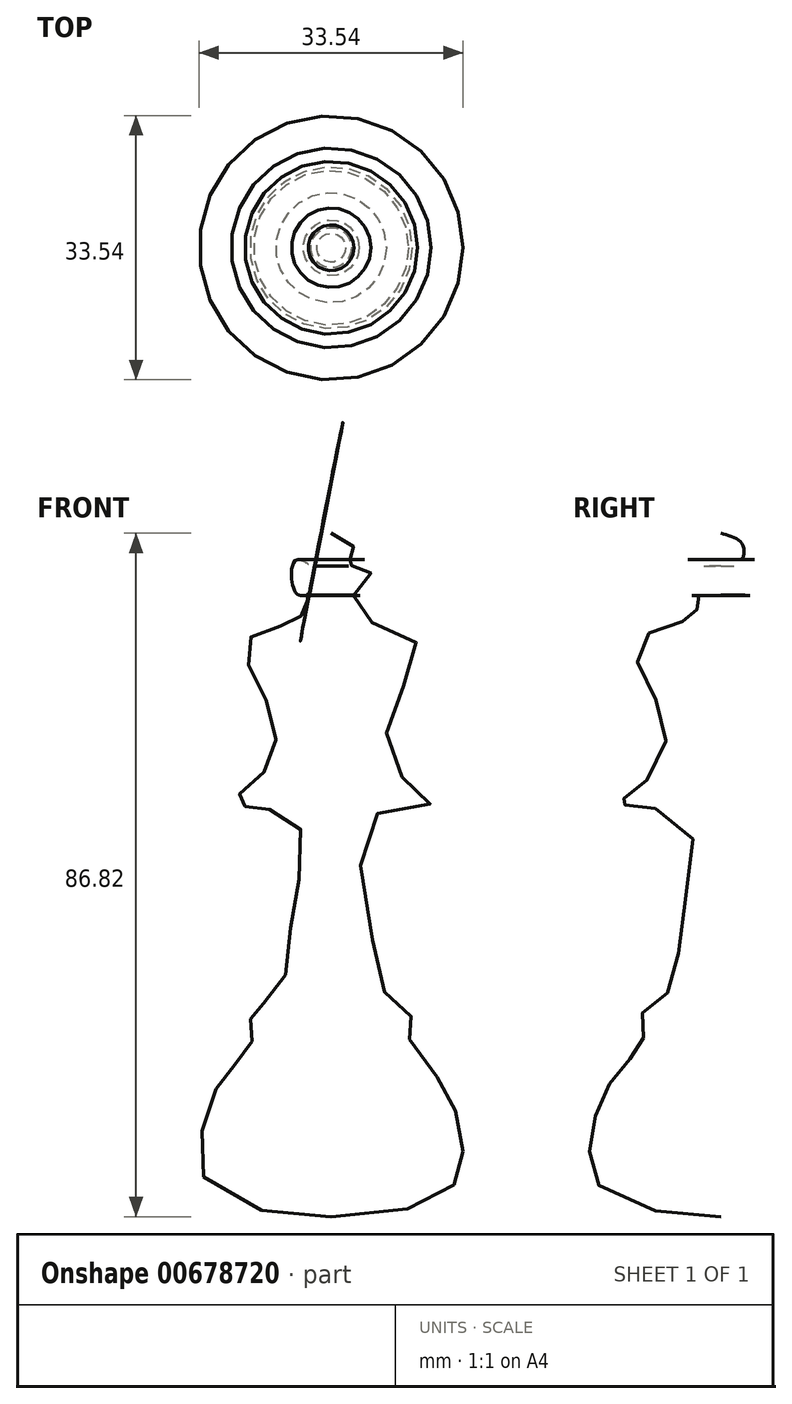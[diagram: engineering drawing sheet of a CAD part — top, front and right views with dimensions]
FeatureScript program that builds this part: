
annotation { "Feature Type Name" : "Feature", "Feature Type Description" : "" }
export const myFeature = defineFeature(function(context is Context, id is Id, definition is map)
    precondition{}
    {
        {
            var Q0;
            Q0=qCreatedBy(makeId("Front.planeOp"),FACE);
            var sketch = newSketch(context, id + "F0", { "sketchPlane" : qUnion([Q0])});
            skFitSpline(sketch, "E0", {"points": [v(0, 66.18) * mm, v(2.46, 65.16) * mm, v(2.88, 64.25) * mm, v(2.9, 63.57) * mm, v(2.76, 63.07) * mm, v(2.2, 62.77) * mm, v(1.89, 62.77) * mm, v(1.96, 62.1) * mm, v(2.72, 62.17) * mm, v(4.59, 62.72) * mm, v(4.35, 58.48) * mm, v(2.74, 58.25) * mm, v(3.92, 55.56) * mm, v(10.61, 52.62) * mm, v(9.54, 47.53) * mm, v(7.02, 40.7) * mm, v(9.43, 34.81) * mm, v(12.64, 31.87) * mm, v(4.88, 30) * mm, v(4.9, 17.88) * mm, v(6.66, 8) * mm, v(9.84, 5.46) * mm, v(10.16, 3.23) * mm, v(9.84, 2.28) * mm, v(13.03, -2.34) * mm, v(15.42, -6) * mm, v(16.6, -11.18) * mm, v(16.6, -14.4) * mm, v(13.8, -18.23) * mm, v(0, -20.64) * mm], "startDerivative": vector(99.64, -28.35) * mm, "endDerivative": vector(-237.87, -14.2) * mm});
            skLineSegment(sketch, "E1", {"start": v(0, -20.64) * mm, "end": v(0, 66.18) * mm, "construction": true});
            skSolve(sketch);
        }
        {
            var Q0;
            Q0=sQuery(id+"F0.wireOp",EDGE,"E1");
            var Q1;
            Q1=sQuery(id+"F0.wireOp",EDGE,"E0");
            var Q2;
            Q2=sQuery(id+"F0.wireOp",EDGE,"E1");
            revolve(context, id + "F1", {"bodyType" : ToolBodyType.SURFACE, "surfaceEntities" : qUnion([Q0, Q1]), "axis" : qUnion([Q2]), "revolveType" : RevolveType.FULL});
        }
    });
